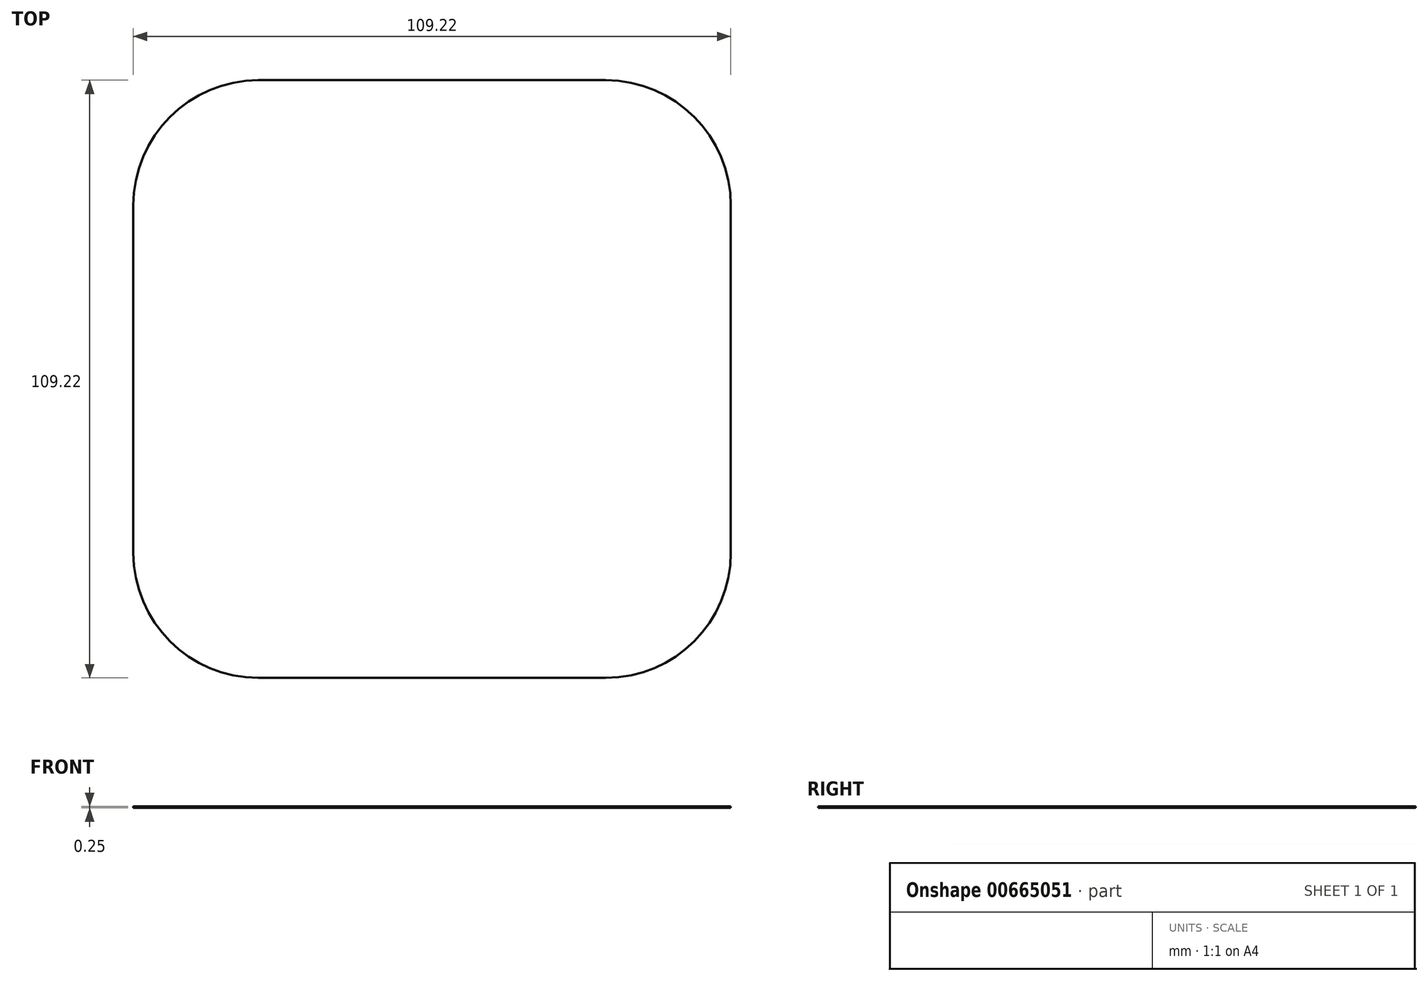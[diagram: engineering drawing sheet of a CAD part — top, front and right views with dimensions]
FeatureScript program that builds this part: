
annotation { "Feature Type Name" : "Feature", "Feature Type Description" : "" }
export const myFeature = defineFeature(function(context is Context, id is Id, definition is map)
    precondition{}
    {
        {
            var Q0;
            Q0=qCreatedBy(makeId("Top.planeOp"),FACE);
            var sketch = newSketch(context, id + "F0", { "sketchPlane" : qUnion([Q0])});
            skLineSegment(sketch, "E0.bottom", {"start": v(31.75, 54.61) * mm, "end": v(-31.75, 54.61) * mm});
            skLineSegment(sketch, "E0.top", {"start": v(31.75, -54.61) * mm, "end": v(-31.75, -54.61) * mm});
            skLineSegment(sketch, "E0.left", {"start": v(54.61, 31.75) * mm, "end": v(54.61, -31.75) * mm});
            skLineSegment(sketch, "E0.right", {"start": v(-54.61, 31.75) * mm, "end": v(-54.61, -31.75) * mm});
            skPoint(sketch, "E0.middle", {"position": v(0, 0) * mm});
            skPoint(sketch, "E1.visualSharp", {"position": v(-54.61, 54.61) * mm});
            skArc(sketch, "E1.filletArc", {"start": v(-31.75, 54.61) * mm, "mid": v(-47.91, 47.91) * mm, "end": v(-54.61, 31.75) * mm});
            skPoint(sketch, "E2.visualSharp", {"position": v(54.61, 54.61) * mm});
            skArc(sketch, "E2.filletArc", {"start": v(54.61, 31.75) * mm, "mid": v(47.91, 47.91) * mm, "end": v(31.75, 54.61) * mm});
            skPoint(sketch, "E3.visualSharp", {"position": v(54.61, -54.61) * mm});
            skArc(sketch, "E3.filletArc", {"start": v(31.75, -54.61) * mm, "mid": v(47.91, -47.91) * mm, "end": v(54.61, -31.75) * mm});
            skPoint(sketch, "E4.visualSharp", {"position": v(-54.6, -54.61) * mm});
            skArc(sketch, "E4.filletArc", {"start": v(-54.61, -31.75) * mm, "mid": v(-47.91, -47.91) * mm, "end": v(-31.75, -54.61) * mm});
            skSolve(sketch);
        }
        {
            var Q0;
            Q0 = qSketchRegion(id + "F0", true);
            extrude(context, id + "F1", {"entities" : qUnion([Q0]), "depth" : 0.25 * mm, "offsetDistance" : 25.4 * mm});
        }
    });
